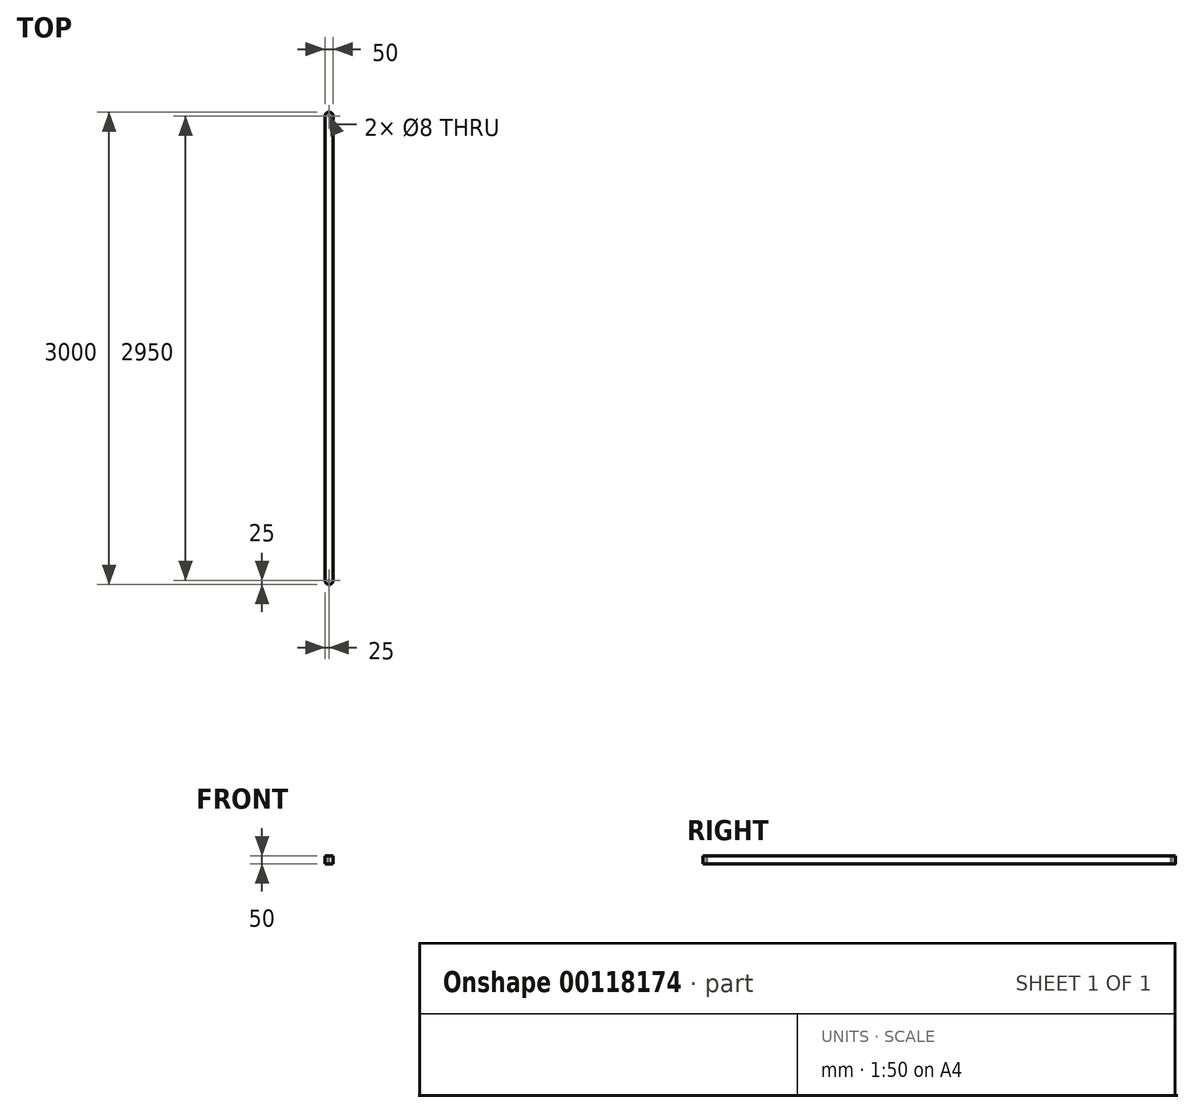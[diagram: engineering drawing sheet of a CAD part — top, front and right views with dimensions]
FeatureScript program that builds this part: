
annotation { "Feature Type Name" : "Feature", "Feature Type Description" : "" }
export const myFeature = defineFeature(function(context is Context, id is Id, definition is map)
    precondition{}
    {
        {
            var Q0;
            Q0=qCreatedBy(makeId("Front.planeOp"),FACE);
            var sketch = newSketch(context, id + "F0", { "sketchPlane" : qUnion([Q0])});
            skLineSegment(sketch, "E0.bottom", {"start": v(0, 0) * mm, "end": v(50, 0) * mm});
            skLineSegment(sketch, "E0.top", {"start": v(0, 50) * mm, "end": v(50, 50) * mm});
            skLineSegment(sketch, "E0.left", {"start": v(0, 0) * mm, "end": v(0, 50) * mm});
            skLineSegment(sketch, "E0.right", {"start": v(50, 0) * mm, "end": v(50, 50) * mm});
            skSolve(sketch);
        }
        {
            var Q0;
            Q0=makeQuery(id+"F0.imprint","IMPRINT",FACE,{"disambiguationData":[TD([[makeQuery(id+"F0.imprint","IMPRINT",EDGE,{"derivedFrom":sQuery(id+"F0.wireOp",EDGE,"E0.bottom")}),1.0]])]});
            extrude(context, id + "F1", {"entities" : qUnion([Q0]), "depth" : 3000 * mm});
        }
        {
            var Q0;
            Q0=makeQuery(id+"F1.opExtrude","SWEPT_FACE",FACE,{"disambiguationData":[OSD([sQuery(id+"F0.wireOp",EDGE,"E0.top")])]});
            var sketch = newSketch(context, id + "F2", { "sketchPlane" : qUnion([Q0])});
            skPoint(sketch, "E1.endSnap0", {"position": v(25, 0) * mm});
            skCircle(sketch, "E2", {"center": v(25, -25) * mm, "radius": 4 * mm});
            skCircle(sketch, "E3", {"center": v(25, -2975) * mm, "radius": 4 * mm});
            skSolve(sketch);
        }
        {
            var Q0;
            Q0 = qSketchRegion(id + "F2", true);
            extrude(context, id + "F3", {"entities" : qUnion([Q0]), "operationType" : NewBodyOperationType.REMOVE, "endBound" : BoundingType.THROUGH_ALL, "oppositeDirection" : true, "depth" : 25 * mm});
        }
        {
            var Q0;
            Q0=makeQuery(id+"F1.opExtrude","SWEPT_FACE",FACE,{"disambiguationData":[OSD([sQuery(id+"F0.wireOp",EDGE,"E0.top")])]});
            var sketch = newSketch(context, id + "F4", { "sketchPlane" : qUnion([Q0])});
            skArc(sketch, "E4", {"start": v(50, -25) * mm, "mid": v(25, 0) * mm, "end": v(0, -25) * mm});
            skArc(sketch, "E5", {"start": v(0, -2975) * mm, "mid": v(25, -3000) * mm, "end": v(50, -2975) * mm});
            skLineSegment(sketch, "E6.top", {"start": v(50, -3000) * mm, "end": v(0, -3000) * mm});
            skLineSegment(sketch, "E6.left", {"start": v(50, -2975) * mm, "end": v(50, -3000) * mm});
            skLineSegment(sketch, "E6.right", {"start": v(0, -2975) * mm, "end": v(0, -3000) * mm});
            skLineSegment(sketch, "E7.top", {"start": v(0, 0) * mm, "end": v(50, 0) * mm});
            skLineSegment(sketch, "E7.left", {"start": v(0, -25) * mm, "end": v(0, 0) * mm});
            skLineSegment(sketch, "E7.right", {"start": v(50, -25) * mm, "end": v(50, 0) * mm});
            skSolve(sketch);
        }
        {
            var Q0;
            Q0 = qSketchRegion(id + "F4", true);
            extrude(context, id + "F5", {"entities" : qUnion([Q0]), "operationType" : NewBodyOperationType.REMOVE, "endBound" : BoundingType.UP_TO_NEXT, "oppositeDirection" : true, "depth" : 25 * mm});
        }
    });
